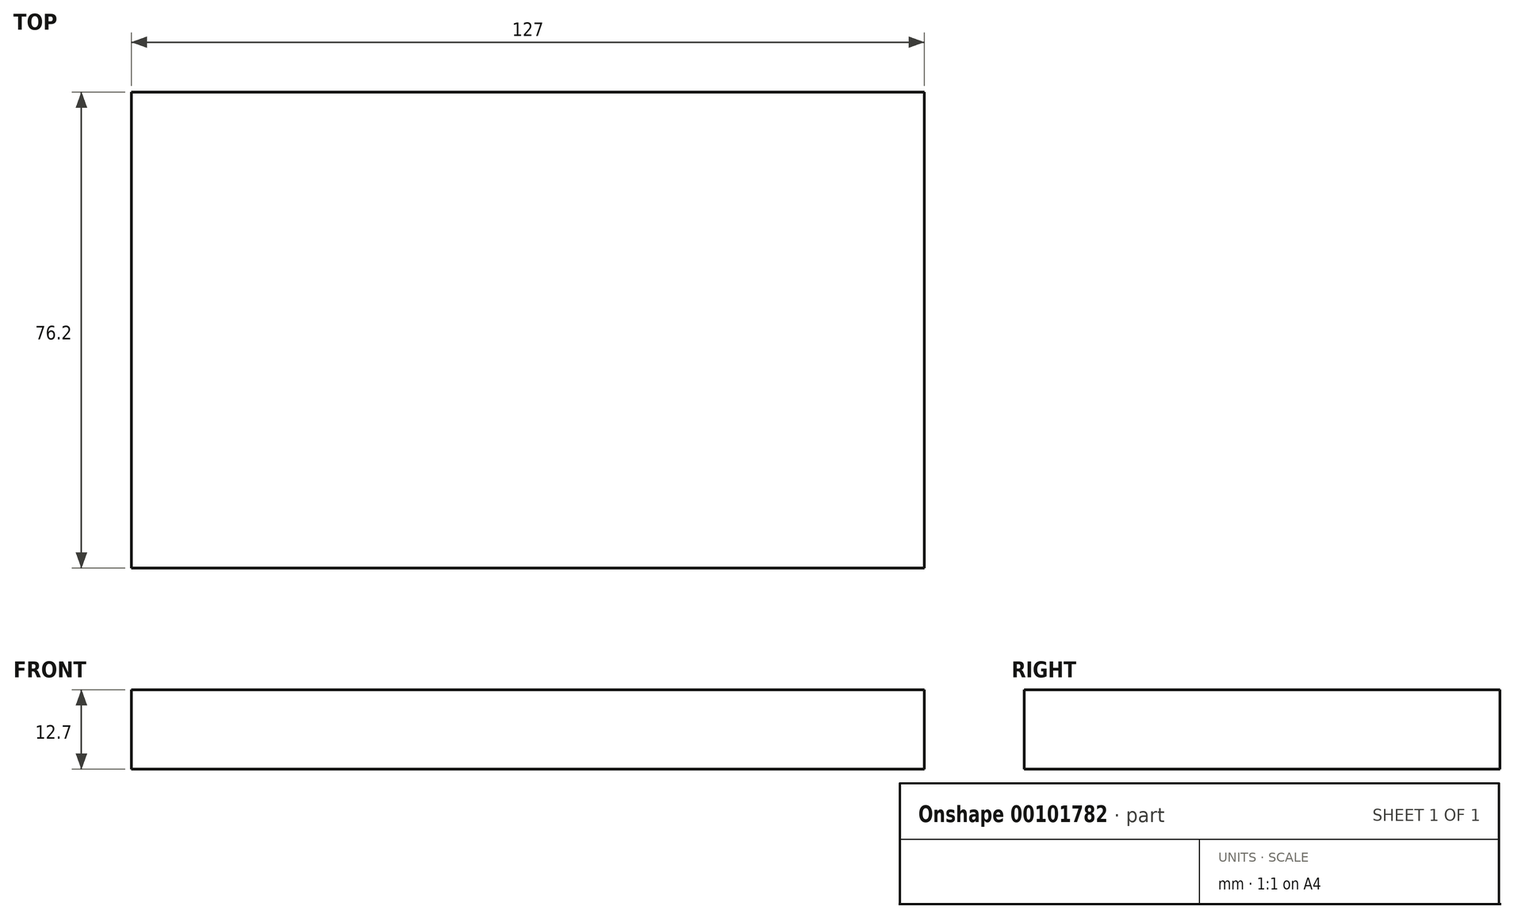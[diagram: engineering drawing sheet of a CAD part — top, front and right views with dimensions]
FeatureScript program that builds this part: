
annotation { "Feature Type Name" : "Feature", "Feature Type Description" : "" }
export const myFeature = defineFeature(function(context is Context, id is Id, definition is map)
    precondition{}
    {
        {
            var Q0;
            Q0=qCreatedBy(makeId("Top.planeOp"),FACE);
            var sketch = newSketch(context, id + "F0", { "sketchPlane" : qUnion([Q0])});
            skLineSegment(sketch, "E0.bottom", {"start": v(-73, 28.37) * mm, "end": v(54, 28.37) * mm});
            skLineSegment(sketch, "E0.top", {"start": v(-73, -47.83) * mm, "end": v(54, -47.83) * mm});
            skLineSegment(sketch, "E0.left", {"start": v(-73, 28.37) * mm, "end": v(-73, -47.83) * mm});
            skLineSegment(sketch, "E0.right", {"start": v(54, 28.37) * mm, "end": v(54, -47.83) * mm});
            skSolve(sketch);
        }
        {
            var Q0;
            Q0=makeQuery(id+"F0.imprint","IMPRINT",FACE,{"disambiguationData":[TD([[makeQuery(id+"F0.imprint","IMPRINT",EDGE,{"derivedFrom":sQuery(id+"F0.wireOp",EDGE,"E0.bottom")}),-1.0]])]});
            extrude(context, id + "F1", {"entities" : qUnion([Q0]), "depth" : 12.7 * mm});
        }
    });
